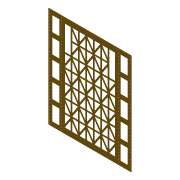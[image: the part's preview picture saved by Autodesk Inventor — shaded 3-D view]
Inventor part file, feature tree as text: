
AUTODESK INVENTOR PART (.ipt)
format: ipt  version: 2015 (Build 190159000, 159)  size: 1,641,984 bytes
history: native  units: in
note: dims shown in document units (in); Inventor stores cm internally (conversion verified against a paired STEP export)
features: sketch x4, fillet x2, other x2, extrude x1, hole x1
ambient origin geometry x8: Origin, YZ Plane, XZ Plane, XY Plane, X Axis, Y Axis, Z Axis, Center Point
bodies: Solid1 (feature_tree)
feature tree (10):
  extrude  "Extrusion1"  Depth=34.0in
  hole  "Hole1"  [1 undecoded]
  fillet  "Fillet1"  Radius=2.0in
  fillet  "Fillet2"  Radius=3.0in
  sketch  "Sketch1"  dims[d0=28.0in d1=34.0in]
  sketch  "Sketch2"  dims[d2=2.0in d3=3.0in d4=2.0in d5=3.0in]
  sketch  "Sketch3"  dims[d6=0.901in]
  sketch  "Sketch4"  dims[d7=5.5in d8=1.8465in d9=0.25in d10=0.125in d11=0.25in d12=1.1811in d14=5.0in d15=1.1811in d17=8.802in d20=0.25in d22=3.0in d23=2.0in d24=0.901in d25=2.0in d26=0.5in d27=0.125in d28=1.1811in d30=5.0in d31=0.3937in d33=1.0in d35=0.09in d36=0.0in d37=0.5in d38=4.5in d39=4.5in d40=0.5in d41=0.5in d42=13.3858in d44=1.0in d45=0.3937in d47=1.0in d49=0.266in d50=0.75in d51=0.375in d52=0.25in d53=0.5635in d54=0.12in d55=0.8108in d56=1.25in d57=1.5in d58=3.75in d59=5.0in d60=0.125in d61=1.9685in d63=6.5in d64=0.7874in d66=23.0in d69=0.12in d70=0.0in d71=0.0in d72=0.0in d73=0.0in d74=0.0in d75=0.125in d76=14.0in d77=0.0in d78=0.0in d79=0.0in d80=0.125in d81=0.12in d82=0.0in d83=0.125in d84=0.125in]
  other  "Cut1"
  other  "Cut2"
note: 1 required parameter value undecoded (feature->parameter linkage not recoverable at this tier; creation-order binding heuristic only, values carry confidence <= 0.55)
